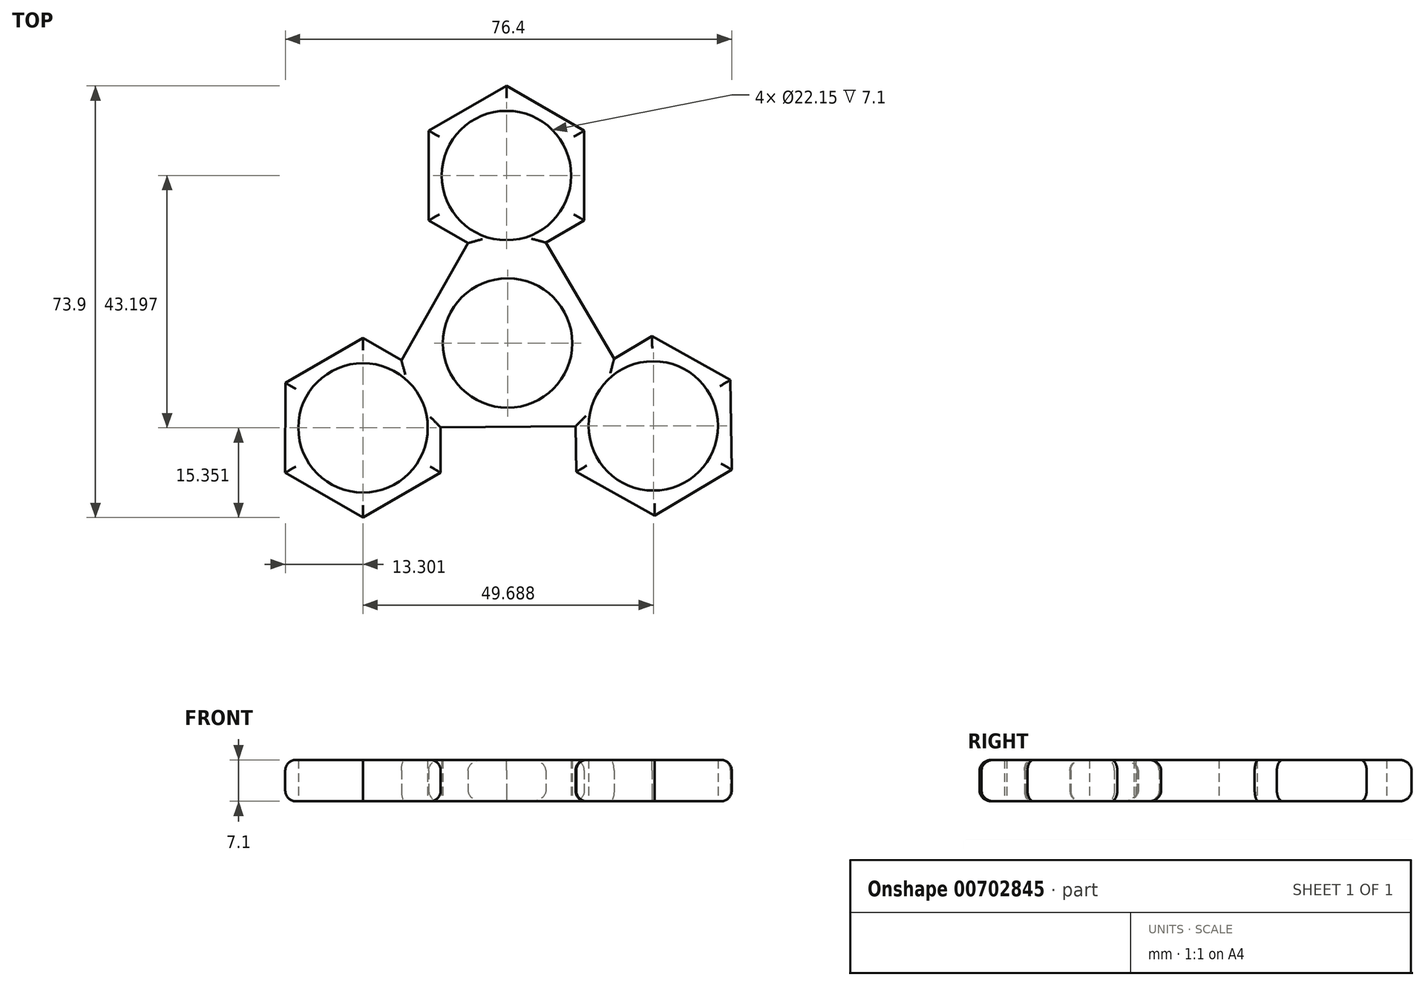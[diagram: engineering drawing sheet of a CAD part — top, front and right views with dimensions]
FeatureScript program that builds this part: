
annotation { "Feature Type Name" : "Feature", "Feature Type Description" : "" }
export const myFeature = defineFeature(function(context is Context, id is Id, definition is map)
    precondition{}
    {
        {
            var Q0;
            Q0=qCreatedBy(makeId("Top.planeOp"),FACE);
            var sketch = newSketch(context, id + "F0", { "sketchPlane" : qUnion([Q0])});
            skCircle(sketch, "E0.cCircle", {"center": v(0, 0) * mm, "radius": 14.34 * mm, "construction": true});
            skLineSegment(sketch, "E0.0", {"start": v(-0.2, 28.69) * mm, "end": v(24.94, -14.18) * mm});
            skLineSegment(sketch, "E0.1", {"start": v(24.94, -14.18) * mm, "end": v(-24.75, -14.5) * mm});
            skLineSegment(sketch, "E0.2", {"start": v(-24.75, -14.5) * mm, "end": v(-0.2, 28.69) * mm});
            skPoint(sketch, "E0.0.midPoint", {"position": v(12.37, 7.25) * mm});
            skCircle(sketch, "E1.cCircle", {"center": v(-0.2, 28.69) * mm, "radius": 13.3 * mm, "construction": true});
            skLineSegment(sketch, "E1.0", {"start": v(13.1, 36.37) * mm, "end": v(13.1, 21.01) * mm});
            skLineSegment(sketch, "E1.1", {"start": v(13.1, 21.01) * mm, "end": v(-0.2, 13.33) * mm});
            skLineSegment(sketch, "E1.2", {"start": v(-0.2, 13.33) * mm, "end": v(-13.49, 21.01) * mm});
            skLineSegment(sketch, "E1.3", {"start": v(-13.49, 21.01) * mm, "end": v(-13.49, 36.37) * mm});
            skLineSegment(sketch, "E1.4", {"start": v(-13.49, 36.37) * mm, "end": v(-0.2, 44.04) * mm});
            skLineSegment(sketch, "E1.5", {"start": v(-0.2, 44.04) * mm, "end": v(13.1, 36.37) * mm});
            skPoint(sketch, "E1.0.midPoint", {"position": v(13.1, 28.69) * mm});
            skCircle(sketch, "E2.cCircle", {"center": v(24.94, -14.18) * mm, "radius": 13.3 * mm, "construction": true});
            skLineSegment(sketch, "E2.0", {"start": v(38.13, -6.31) * mm, "end": v(38.35, -21.67) * mm});
            skLineSegment(sketch, "E2.1", {"start": v(38.35, -21.67) * mm, "end": v(25.16, -29.53) * mm});
            skLineSegment(sketch, "E2.2", {"start": v(25.16, -29.53) * mm, "end": v(11.75, -22.04) * mm});
            skLineSegment(sketch, "E2.3", {"start": v(11.75, -22.04) * mm, "end": v(11.53, -6.7) * mm});
            skLineSegment(sketch, "E2.4", {"start": v(11.53, -6.7) * mm, "end": v(24.72, 1.18) * mm});
            skLineSegment(sketch, "E2.5", {"start": v(24.72, 1.18) * mm, "end": v(38.13, -6.31) * mm});
            skPoint(sketch, "E2.0.midPoint", {"position": v(38.24, -13.99) * mm});
            skCircle(sketch, "E3.cCircle", {"center": v(-24.75, -14.5) * mm, "radius": 13.3 * mm, "construction": true});
            skLineSegment(sketch, "E3.0", {"start": v(-24.76, -29.86) * mm, "end": v(-38.05, -22.18) * mm});
            skLineSegment(sketch, "E3.1", {"start": v(-38.05, -22.18) * mm, "end": v(-38.04, -6.82) * mm});
            skLineSegment(sketch, "E3.2", {"start": v(-38.04, -6.82) * mm, "end": v(-24.74, 0.85) * mm});
            skLineSegment(sketch, "E3.3", {"start": v(-24.74, 0.85) * mm, "end": v(-11.44, -6.84) * mm});
            skLineSegment(sketch, "E3.4", {"start": v(-11.44, -6.84) * mm, "end": v(-11.46, -22.2) * mm});
            skLineSegment(sketch, "E3.5", {"start": v(-11.46, -22.2) * mm, "end": v(-24.76, -29.86) * mm});
            skPoint(sketch, "E3.0.midPoint", {"position": v(-31.4, -26.02) * mm});
            skCircle(sketch, "E4", {"center": v(-0.2, 28.69) * mm, "radius": 11.07 * mm});
            skCircle(sketch, "E5", {"center": v(0, 0) * mm, "radius": 11.07 * mm});
            skCircle(sketch, "E6", {"center": v(-24.75, -14.5) * mm, "radius": 11.07 * mm});
            skCircle(sketch, "E7", {"center": v(24.94, -14.18) * mm, "radius": 11.07 * mm});
            skSolve(sketch);
        }
        {
            var Q0;
            Q0 = qSketchRegion(id + "F0", true);
            extrude(context, id + "F1", {"entities" : qUnion([Q0]), "depth" : 7.1 * mm, "offsetDistance" : 25 * mm});
        }
        {
            var Q0;
            Q0=makeQuery(id+"F1.opExtrude","CAP_EDGE",EDGE,{"disambiguationData":[OSD([sQuery(id+"F0.wireOp",EDGE,"E3.5")])],"isStart":false});
            var Q1;
            Q1=makeQuery(id+"F1.opExtrude","CAP_EDGE",EDGE,{"disambiguationData":[OSD([sQuery(id+"F0.wireOp",EDGE,"E0.1")])],"isStart":false});
            var Q2;
            Q2=makeQuery(id+"F1.opExtrude","CAP_EDGE",EDGE,{"disambiguationData":[OSD([sQuery(id+"F0.wireOp",EDGE,"E2.2")])],"isStart":false});
            var Q3;
            Q3=makeQuery(id+"F1.opExtrude","CAP_EDGE",EDGE,{"disambiguationData":[OSD([sQuery(id+"F0.wireOp",EDGE,"E2.1")])],"isStart":false});
            var Q4;
            Q4=makeQuery(id+"F1.opExtrude","CAP_EDGE",EDGE,{"disambiguationData":[OSD([sQuery(id+"F0.wireOp",EDGE,"E2.0")])],"isStart":false});
            var Q5;
            Q5=makeQuery(id+"F1.opExtrude","CAP_EDGE",EDGE,{"disambiguationData":[OSD([sQuery(id+"F0.wireOp",EDGE,"E2.5")])],"isStart":false});
            var Q6;
            Q6=makeQuery(id+"F1.opExtrude","CAP_EDGE",EDGE,{"disambiguationData":[OSD([sQuery(id+"F0.wireOp",EDGE,"E2.4")])],"isStart":false});
            var Q7;
            Q7=makeQuery(id+"F1.opExtrude","CAP_EDGE",EDGE,{"disambiguationData":[OSD([sQuery(id+"F0.wireOp",EDGE,"E0.0")])],"isStart":false});
            var Q8;
            Q8=makeQuery(id+"F1.opExtrude","CAP_EDGE",EDGE,{"disambiguationData":[OSD([sQuery(id+"F0.wireOp",EDGE,"E3.0")])],"isStart":false});
            var Q9;
            Q9=makeQuery(id+"F1.opExtrude","CAP_EDGE",EDGE,{"disambiguationData":[OSD([sQuery(id+"F0.wireOp",EDGE,"E3.1")])],"isStart":false});
            var Q10;
            Q10=makeQuery(id+"F1.opExtrude","CAP_EDGE",EDGE,{"disambiguationData":[OSD([sQuery(id+"F0.wireOp",EDGE,"E3.2")])],"isStart":false});
            var Q11;
            Q11=makeQuery(id+"F1.opExtrude","CAP_EDGE",EDGE,{"disambiguationData":[OSD([sQuery(id+"F0.wireOp",EDGE,"E3.3")])],"isStart":false});
            var Q12;
            Q12=makeQuery(id+"F1.opExtrude","CAP_EDGE",EDGE,{"disambiguationData":[OSD([sQuery(id+"F0.wireOp",EDGE,"E0.2")])],"isStart":false});
            var Q13;
            Q13=makeQuery(id+"F1.opExtrude","CAP_EDGE",EDGE,{"disambiguationData":[OSD([sQuery(id+"F0.wireOp",EDGE,"E1.2")])],"isStart":false});
            var Q14;
            Q14=makeQuery(id+"F1.opExtrude","CAP_EDGE",EDGE,{"disambiguationData":[OSD([sQuery(id+"F0.wireOp",EDGE,"E1.3")])],"isStart":false});
            var Q15;
            Q15=makeQuery(id+"F1.opExtrude","CAP_EDGE",EDGE,{"disambiguationData":[OSD([sQuery(id+"F0.wireOp",EDGE,"E1.4")])],"isStart":false});
            var Q16;
            Q16=makeQuery(id+"F1.opExtrude","CAP_EDGE",EDGE,{"disambiguationData":[OSD([sQuery(id+"F0.wireOp",EDGE,"E1.5")])],"isStart":false});
            var Q17;
            Q17=makeQuery(id+"F1.opExtrude","CAP_EDGE",EDGE,{"disambiguationData":[OSD([sQuery(id+"F0.wireOp",EDGE,"E1.0")])],"isStart":false});
            var Q18;
            Q18=makeQuery(id+"F1.opExtrude","CAP_EDGE",EDGE,{"disambiguationData":[OSD([sQuery(id+"F0.wireOp",EDGE,"E1.1")])],"isStart":false});
            var Q19;
            Q19=makeQuery(id+"F1.opExtrude","CAP_EDGE",EDGE,{"disambiguationData":[OSD([sQuery(id+"F0.wireOp",EDGE,"E2.5")])],"isStart":true});
            var Q20;
            Q20=makeQuery(id+"F1.opExtrude","CAP_EDGE",EDGE,{"disambiguationData":[OSD([sQuery(id+"F0.wireOp",EDGE,"E2.4")])],"isStart":true});
            var Q21;
            Q21=makeQuery(id+"F1.opExtrude","CAP_EDGE",EDGE,{"disambiguationData":[OSD([sQuery(id+"F0.wireOp",EDGE,"E0.0")])],"isStart":true});
            var Q22;
            Q22=makeQuery(id+"F1.opExtrude","CAP_EDGE",EDGE,{"disambiguationData":[OSD([sQuery(id+"F0.wireOp",EDGE,"E1.1")])],"isStart":true});
            var Q23;
            Q23=makeQuery(id+"F1.opExtrude","CAP_EDGE",EDGE,{"disambiguationData":[OSD([sQuery(id+"F0.wireOp",EDGE,"E1.0")])],"isStart":true});
            var Q24;
            Q24=makeQuery(id+"F1.opExtrude","CAP_EDGE",EDGE,{"disambiguationData":[OSD([sQuery(id+"F0.wireOp",EDGE,"E1.5")])],"isStart":true});
            var Q25;
            Q25=makeQuery(id+"F1.opExtrude","CAP_EDGE",EDGE,{"disambiguationData":[OSD([sQuery(id+"F0.wireOp",EDGE,"E1.4")])],"isStart":true});
            var Q26;
            Q26=makeQuery(id+"F1.opExtrude","CAP_EDGE",EDGE,{"disambiguationData":[OSD([sQuery(id+"F0.wireOp",EDGE,"E1.3")])],"isStart":true});
            var Q27;
            Q27=makeQuery(id+"F1.opExtrude","CAP_EDGE",EDGE,{"disambiguationData":[OSD([sQuery(id+"F0.wireOp",EDGE,"E1.2")])],"isStart":true});
            var Q28;
            Q28=makeQuery(id+"F1.opExtrude","CAP_EDGE",EDGE,{"disambiguationData":[OSD([sQuery(id+"F0.wireOp",EDGE,"E0.2")])],"isStart":true});
            var Q29;
            Q29=makeQuery(id+"F1.opExtrude","CAP_EDGE",EDGE,{"disambiguationData":[OSD([sQuery(id+"F0.wireOp",EDGE,"E3.3")])],"isStart":true});
            var Q30;
            Q30=makeQuery(id+"F1.opExtrude","CAP_EDGE",EDGE,{"disambiguationData":[OSD([sQuery(id+"F0.wireOp",EDGE,"E3.2")])],"isStart":true});
            var Q31;
            Q31=makeQuery(id+"F1.opExtrude","CAP_EDGE",EDGE,{"disambiguationData":[OSD([sQuery(id+"F0.wireOp",EDGE,"E3.1")])],"isStart":true});
            var Q32;
            Q32=makeQuery(id+"F1.opExtrude","CAP_EDGE",EDGE,{"disambiguationData":[OSD([sQuery(id+"F0.wireOp",EDGE,"E3.0")])],"isStart":true});
            var Q33;
            Q33=makeQuery(id+"F1.opExtrude","CAP_EDGE",EDGE,{"disambiguationData":[OSD([sQuery(id+"F0.wireOp",EDGE,"E3.5")])],"isStart":true});
            var Q34;
            Q34=makeQuery(id+"F1.opExtrude","CAP_EDGE",EDGE,{"disambiguationData":[OSD([sQuery(id+"F0.wireOp",EDGE,"E3.4")])],"isStart":true});
            var Q35;
            Q35=makeQuery(id+"F1.opExtrude","CAP_EDGE",EDGE,{"disambiguationData":[OSD([sQuery(id+"F0.wireOp",EDGE,"E0.1")])],"isStart":true});
            var Q36;
            Q36=makeQuery(id+"F1.opExtrude","CAP_EDGE",EDGE,{"disambiguationData":[OSD([sQuery(id+"F0.wireOp",EDGE,"E2.3")])],"isStart":true});
            var Q37;
            Q37=makeQuery(id+"F1.opExtrude","CAP_EDGE",EDGE,{"disambiguationData":[OSD([sQuery(id+"F0.wireOp",EDGE,"E2.2")])],"isStart":true});
            var Q38;
            Q38=makeQuery(id+"F1.opExtrude","CAP_EDGE",EDGE,{"disambiguationData":[OSD([sQuery(id+"F0.wireOp",EDGE,"E2.1")])],"isStart":true});
            var Q39;
            Q39=makeQuery(id+"F1.opExtrude","CAP_EDGE",EDGE,{"disambiguationData":[OSD([sQuery(id+"F0.wireOp",EDGE,"E2.0")])],"isStart":true});
            var Q40;
            Q40=makeQuery(id+"F1.opExtrude","CAP_EDGE",EDGE,{"disambiguationData":[OSD([sQuery(id+"F0.wireOp",EDGE,"E3.4")])],"isStart":false});
            var Q41;
            Q41=makeQuery(id+"F1.opExtrude","CAP_EDGE",EDGE,{"disambiguationData":[OSD([sQuery(id+"F0.wireOp",EDGE,"E2.3")])],"isStart":false});
            fillet(context, id + "F2", {"entities" : qUnion([Q0, Q1, Q2, Q3, Q4, Q5, Q6, Q7, Q8, Q9, Q10, Q11, Q12, Q13, Q14, Q15, Q16, Q17, Q18, Q19, Q20, Q21, Q22, Q23, Q24, Q25, Q26, Q27, Q28, Q29, Q30, Q31, Q32, Q33, Q34, Q35, Q36, Q37, Q38, Q39, Q40, Q41]), "radius" : 1.8 * mm, "tangentPropagation" : true, "allowEdgeOverflow" : false});
        }
    });
